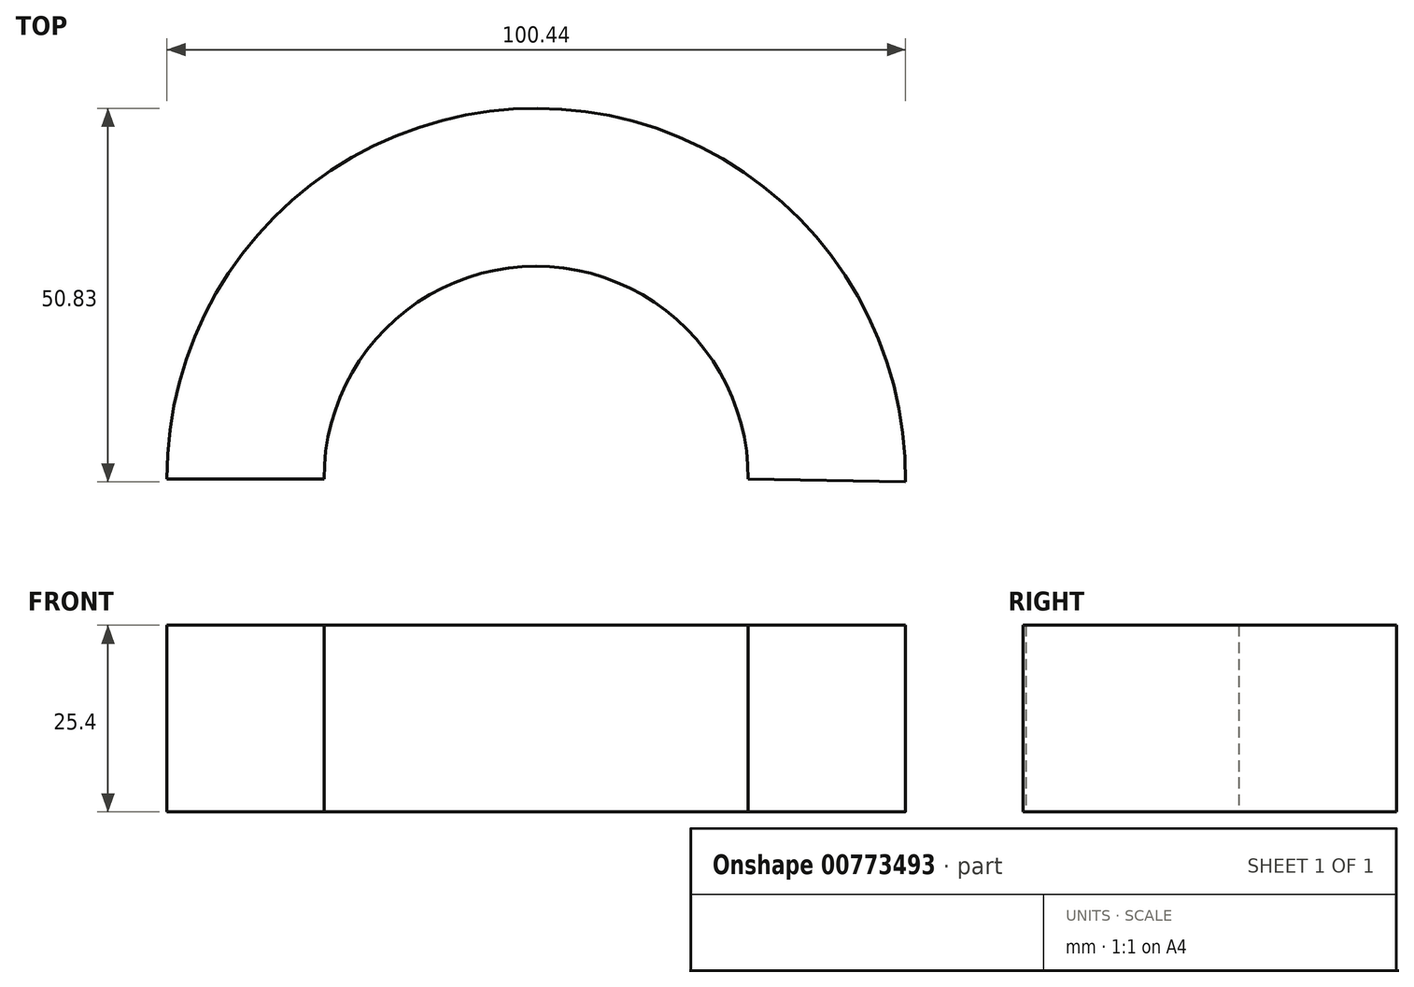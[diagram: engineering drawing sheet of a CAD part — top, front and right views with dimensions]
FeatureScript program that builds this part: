
annotation { "Feature Type Name" : "Feature", "Feature Type Description" : "" }
export const myFeature = defineFeature(function(context is Context, id is Id, definition is map)
    precondition{}
    {
        {
            var Q0;
            Q0=qCreatedBy(makeId("Top.planeOp"),FACE);
            var sketch = newSketch(context, id + "F0", { "sketchPlane" : qUnion([Q0])});
            skLineSegment(sketch, "E0", {"start": v(0, 0) * mm, "end": v(-21.37, 0) * mm});
            skArc(sketch, "E1", {"start": v(57.7, 0) * mm, "mid": v(28.85, 28.97) * mm, "end": v(0, 0) * mm});
            skLineSegment(sketch, "E2", {"start": v(79.06, -0.37) * mm, "end": v(57.7, -0.37) * mm});
            skArc(sketch, "E3", {"start": v(79.06, -0.37) * mm, "mid": v(29.03, 50.46) * mm, "end": v(-21.37, 0) * mm});
            skLineSegment(sketch, "E4", {"start": v(-21.37, 0) * mm, "end": v(0, 0) * mm});
            skLineSegment(sketch, "E5", {"start": v(57.7, 0) * mm, "end": v(79.06, -0.37) * mm});
            skSolve(sketch);
        }
        {
            var Q0;
            Q0=makeQuery(id+"F0.imprint","IMPRINT",FACE,{"disambiguationData":[TD([[makeQuery(id+"F0.imprint","IMPRINT",EDGE,{"derivedFrom":sQuery(id+"F0.wireOp",EDGE,"E1")}),-1.0]])]});
            var Q1;
            Q1 = qSketchRegion(id + "F0", true);
            extrude(context, id + "F1", {"entities" : qUnion([Q0, Q1]), "depth" : 25.4 * mm, "offsetDistance" : 25.4 * mm});
        }
    });
